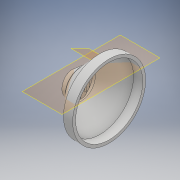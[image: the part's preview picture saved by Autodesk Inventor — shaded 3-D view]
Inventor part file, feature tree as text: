
AUTODESK INVENTOR PART (.ipt)
format: ipt  version: 2018 (Build 220112000, 112)  size: 2,466,304 bytes
history: native  units: mm
features: sketch x73, extrude x64, fillet x27, revolve x3, plane x3, mirror x1
ambient origin geometry x8: Origin, YZ Plane, XZ Plane, XY Plane, X Axis, Y Axis, Z Axis, Center Point
bodies: Solid1 (feature_tree)
feature tree (171):
  extrude  "Extrusion1"  TaperAngle=0.0deg  [1 undecoded]
  extrude  "Extrusion2"  Depth=10.0mm TaperAngle=0.0deg
  extrude  "Extrusion3"  Depth=50.0mm
  extrude  "Extrusion4"  TaperAngle=0.0deg  [1 undecoded]
  extrude  "Extrusion5"  Depth=10.0mm TaperAngle=0.0deg
  sketch  "Sketch6"  dims[d19=10.0mm d20=0.0mm d21=40.0mm]
  extrude  "Extrusion6"  Depth=40.0mm
  extrude  "Extrusion7"  Depth=11.0mm TaperAngle=0.0deg
  extrude  "Extrusion8"  Depth=32.0mm TaperAngle=0.0deg
  extrude  "Extrusion9"  Depth=32.0mm TaperAngle=0.0deg
  extrude  "Extrusion10"  Depth=10.0mm TaperAngle=0.0deg
  extrude  "Extrusion11"  Depth=10.0mm TaperAngle=0.0deg
  extrude  "Extrusion12"  TaperAngle=0.0deg  [1 undecoded]
  extrude  "Extrusion14"  Depth=48.3mm
  extrude  "Extrusion15"  TaperAngle=0.0deg  [1 undecoded]
  extrude  "Extrusion16"  Depth=10.0mm TaperAngle=0.0deg
  extrude  "Extrusion17"  Depth=11.63mm TaperAngle=0.0deg
  sketch  "Sketch21"  dims[d83=0.0mm d84=0.0mm d85=0.0mm d86=0.0mm]
  extrude  "Extrusion19"  Depth=11.63mm TaperAngle=0.0deg
  extrude  "Extrusion20"  TaperAngle=0.0deg  [1 undecoded]
  extrude  "Extrusion21"  Depth=10.0mm TaperAngle=0.0deg
  extrude  "Extrusion22"  TaperAngle=0.0deg  [1 undecoded]
  extrude  "Extrusion23"  Depth=2.86mm TaperAngle=0.0deg
  extrude  "Extrusion24"  Depth=2.01mm
  extrude  "Extrusion25"  Depth=10.0mm TaperAngle=0.0deg
  sketch  "Sketch33"  dims[d115=7.8mm d116=0.0mm d117=0.0mm d118=0.0mm]
  extrude  "Extrusion26"  Depth=7.8mm TaperAngle=0.0deg
  extrude  "Extrusion27"  TaperAngle=0.0deg  [1 undecoded]
  extrude  "Extrusion28"  Depth=22.0mm TaperAngle=0.0deg
  extrude  "Extrusion29"  Depth=17.0mm TaperAngle=0.0deg
  extrude  "Extrusion30"  Depth=2.0mm
  extrude  "Extrusion31"  Depth=6.95mm TaperAngle=0.0deg
  extrude  "Extrusion32"  Depth=18.0mm TaperAngle=0.0deg
  extrude  "Extrusion33"  Depth=1.02mm
  sketch  "Sketch42"  dims[d151=2.0mm d152=2.0mm]
  extrude  "Extrusion34"  Depth=7.72mm TaperAngle=0.0deg
  extrude  "Extrusion36"  Depth=2.0mm
  extrude  "Extrusion37"  Depth=2.0mm
  revolve  "Revolution3"  [1 undecoded]
  extrude  "Extrusion38"  Depth=2.0mm
  extrude  "Extrusion39"  Depth=10.0mm TaperAngle=0.0deg
  fillet  "Fillet1"  Radius=7.83mm
  fillet  "Fillet2"  Radius=20.0mm
  sketch  "Sketch51"  dims[d171=2.0mm d172=2.0mm]
  extrude  "Extrusion41"  Depth=6.4mm TaperAngle=0.0deg
  mirror  "Mirror1"
  extrude  "Extrusion42"  Depth=2.0mm
  sketch  "Sketch54"  dims[d181=2.0mm d182=2.0mm]
  sketch  "Sketch55"  dims[d183=2.0mm d184=2.0mm]
  sketch  "Sketch56"  dims[d185=2.0mm d186=0.0mm d187=0.0mm]
  extrude  "Extrusion44"  Depth=2.0mm
  extrude  "Extrusion45"  Depth=2.0mm
  extrude  "Extrusion46"  TaperAngle=90.0deg  [1 undecoded]
  extrude  "Extrusion47"  Depth=2.0mm
  plane  "Work Plane2"
  extrude  "Extrusion48"  Depth=2.0mm
  extrude  "Extrusion49"  TaperAngle=0.0deg  [1 undecoded]
  plane  "Work Plane5"
  extrude  "Extrusion50"  TaperAngle=0.0deg  [1 undecoded]
  extrude  "Extrusion51"  Depth=15.0mm
  fillet  "Fillet3"  Radius=10.0mm
  fillet  "Fillet4"  Radius=2.0mm
  extrude  "Extrusion52"  Depth=29.0mm
  extrude  "Extrusion53"  Depth=13.7mm
  extrude  "Extrusion54"  [1 undecoded]
  extrude  "Extrusion55"  [1 undecoded]
  fillet  "Fillet5"  [1 undecoded]
  extrude  "Extrusion57"  [1 undecoded]
  extrude  "Extrusion58"  [1 undecoded]
  extrude  "Extrusion59"  [1 undecoded]
  fillet  "Fillet7"  [1 undecoded]
  fillet  "Fillet8"  [1 undecoded]
  fillet  "Fillet9"  [1 undecoded]
  fillet  "Fillet10"  [1 undecoded]
  fillet  "Fillet11"  [1 undecoded]
  fillet  "Fillet12"  [1 undecoded]
  fillet  "Fillet13"  [1 undecoded]
  fillet  "Fillet14"  [1 undecoded]
  extrude  "Extrusion60"  [1 undecoded]
  extrude  "Extrusion61"  [1 undecoded]
  extrude  "Extrusion62"  [1 undecoded]
  extrude  "Extrusion63"  [1 undecoded]
  extrude  "Extrusion64"  [1 undecoded]
  extrude  "Extrusion65"  [1 undecoded]
  fillet  "Fillet15"  [1 undecoded]
  fillet  "Fillet16"  [1 undecoded]
  fillet  "Fillet17"  [1 undecoded]
  fillet  "Fillet18"  [1 undecoded]
  fillet  "Fillet19"  [1 undecoded]
  revolve  "Revolution4"  [1 undecoded]
  fillet  "Fillet20"  [1 undecoded]
  fillet  "Fillet21"  [1 undecoded]
  fillet  "Fillet22"  [1 undecoded]
  fillet  "Fillet23"  [1 undecoded]
  fillet  "Fillet24"  [1 undecoded]
  extrude  "Extrusion66"  [1 undecoded]
  revolve  "Revolution5"  [1 undecoded]
  sketch  "Sketch86"
  extrude  "Extrusion67"  [1 undecoded]
  extrude  "Extrusion68"  [1 undecoded]
  plane  "Work Plane6"
  extrude  "Extrusion69"  [1 undecoded]
  fillet  "Fillet25"  [1 undecoded]
  fillet  "Fillet26"  [1 undecoded]
  extrude  "Extrusion70"  [1 undecoded]
  fillet  "Fillet27"  [1 undecoded]
  fillet  "Fillet28"  [1 undecoded]
  sketch  "Sketch91"
  sketch  "Sketch1"  dims[d0=10.0mm d1=0.0mm d2=0.0mm d3=0.0mm]
  sketch  "Sketch2"  dims[d4=0.0mm d5=0.0mm d6=10.0mm d7=0.0mm]
  sketch  "Sketch3"  dims[d8=10.0mm d9=0.0mm d10=50.0mm]
  sketch  "Sketch4"  dims[d11=10.0mm d12=0.0mm d13=0.0mm d14=0.0mm]
  sketch  "Sketch5"  dims[d15=0.0mm d16=0.0mm d17=10.0mm d18=0.0mm]
  sketch  "Sketch7"  dims[d22=38.0mm d23=11.0mm d24=0.0mm]
  sketch  "Sketch8"  dims[d25=9.5mm d26=0.0mm d33=32.0mm d34=0.0mm]
  sketch  "Sketch9"  dims[d37=32.0mm d38=0.0mm d39=32.0mm d40=0.0mm]
  sketch  "Sketch10"  dims[d41=32.0mm d42=0.0mm d45=10.0mm d46=0.0mm]
  sketch  "Sketch11"  dims[d47=10.0mm d48=0.0mm d49=10.0mm d50=0.0mm]
  sketch  "Sketch12"  dims[d51=0.0mm d52=0.0mm d53=0.0mm d54=0.0mm]
  sketch  "Sketch13"  dims[d65=46.0mm d66=48.3mm]
  sketch  "Sketch16"  dims[d67=9.0mm d68=0.0mm d69=0.0mm d70=0.0mm]
  sketch  "Sketch18"  dims[d71=0.0mm d72=0.0mm d73=10.0mm d74=0.0mm]
  sketch  "Sketch19"  dims[d75=5.0mm d76=0.0mm d77=11.63mm d78=0.0mm]
  sketch  "Sketch20"  dims[d79=11.63mm d80=0.0mm d81=11.63mm d82=0.0mm]
  sketch  "Sketch22"  dims[d87=30.0mm d88=10.0mm d89=0.0mm]
  sketch  "Sketch23"  dims[d92=10.0mm d93=0.0mm d94=0.0mm d95=0.0mm]
  sketch  "Sketch24"  dims[d96=135.0deg d99=2.86mm d100=0.0mm]
  sketch  "Sketch25"  dims[d101=0.0mm d102=0.0mm d105=2.01mm]
  sketch  "Sketch31"  dims[d106=2.22mm d107=10.0mm d108=0.0mm]
  sketch  "Sketch32"  dims[d109=10.0mm d110=0.0mm d113=7.8mm d114=0.0mm]
  sketch  "Sketch34"  dims[d119=16.0mm d120=0.0mm d121=22.0mm d122=0.0mm]
  sketch  "Sketch35"  dims[d123=22.0mm d124=0.0mm d126=17.0mm d127=0.0mm]
  sketch  "Sketch36"  dims[d128=17.0mm d129=0.0mm d130=2.0mm]
  sketch  "Sketch37"  dims[d131=2.0mm d132=6.95mm d133=0.0mm]
  sketch  "Sketch38"  dims[d134=6.95mm d135=0.0mm d136=18.0mm d137=0.0mm]
  sketch  "Sketch39"  dims[d138=16.0mm d139=0.0mm d140=1.02mm]
  sketch  "Sketch40"  dims[d143=15.5mm d144=0.0mm d146=7.72mm d147=0.0mm]
  sketch  "Sketch41"  dims[d148=17.0mm d149=0.0mm d150=2.0mm]
  sketch  "Sketch43"  dims[d153=2.0mm d154=2.0mm]
  sketch  "Sketch45"  dims[d155=2.0mm d156=2.0mm]
  sketch  "Sketch47"  dims[d157=2.0mm d158=10.0mm d159=0.0mm d160=7.83mm d161=0.0mm d162=20.0mm d163=0.0mm]
  sketch  "Sketch48"  dims[d164=0.0mm d165=0.0mm d166=6.4mm d167=0.0mm]
  sketch  "Sketch49"  dims[d168=6.14mm d169=0.0mm d170=2.0mm]
  sketch  "Sketch52"  dims[d173=2.0mm d174=2.0mm]
  sketch  "Sketch53"  dims[d175=1.5mm d176=1.5mm d177=3.0mm d178=10.0mm d180=90.0deg]
  sketch  "Sketch57"  dims[d192=90.0deg d193=0.0mm d194=0.0mm]
  sketch  "Sketch60"  dims[d195=10.0mm d196=0.0mm d197=15.0mm d198=10.0mm d199=0.0mm d200=2.0mm]
  sketch  "Sketch61"  dims[d201=2.0mm d202=29.0mm]
  sketch  "Sketch62"  dims[d203=0.8mm d204=0.0mm d205=13.7mm]
  sketch  "Sketch63"  dims[d206=2.0mm]
  sketch  "Sketch65"
  sketch  "Sketch66"
  sketch  "Sketch67"
  sketch  "Sketch68"
  sketch  "Sketch69"
  sketch  "Sketch70"
  sketch  "Sketch72"
  sketch  "Sketch73"
  sketch  "Sketch74"
  sketch  "Sketch75"
  sketch  "Sketch76"
  sketch  "Sketch78"
  sketch  "Sketch80"
  sketch  "Sketch81"
  sketch  "Sketch82"
  sketch  "Sketch83"
  sketch  "Sketch84"
  sketch  "Sketch85"
  sketch  "Sketch87"
  sketch  "Sketch88"
  sketch  "Sketch89"
note: 52 required parameter values undecoded (feature->parameter linkage not recoverable at this tier; creation-order binding heuristic only, values carry confidence <= 0.55)